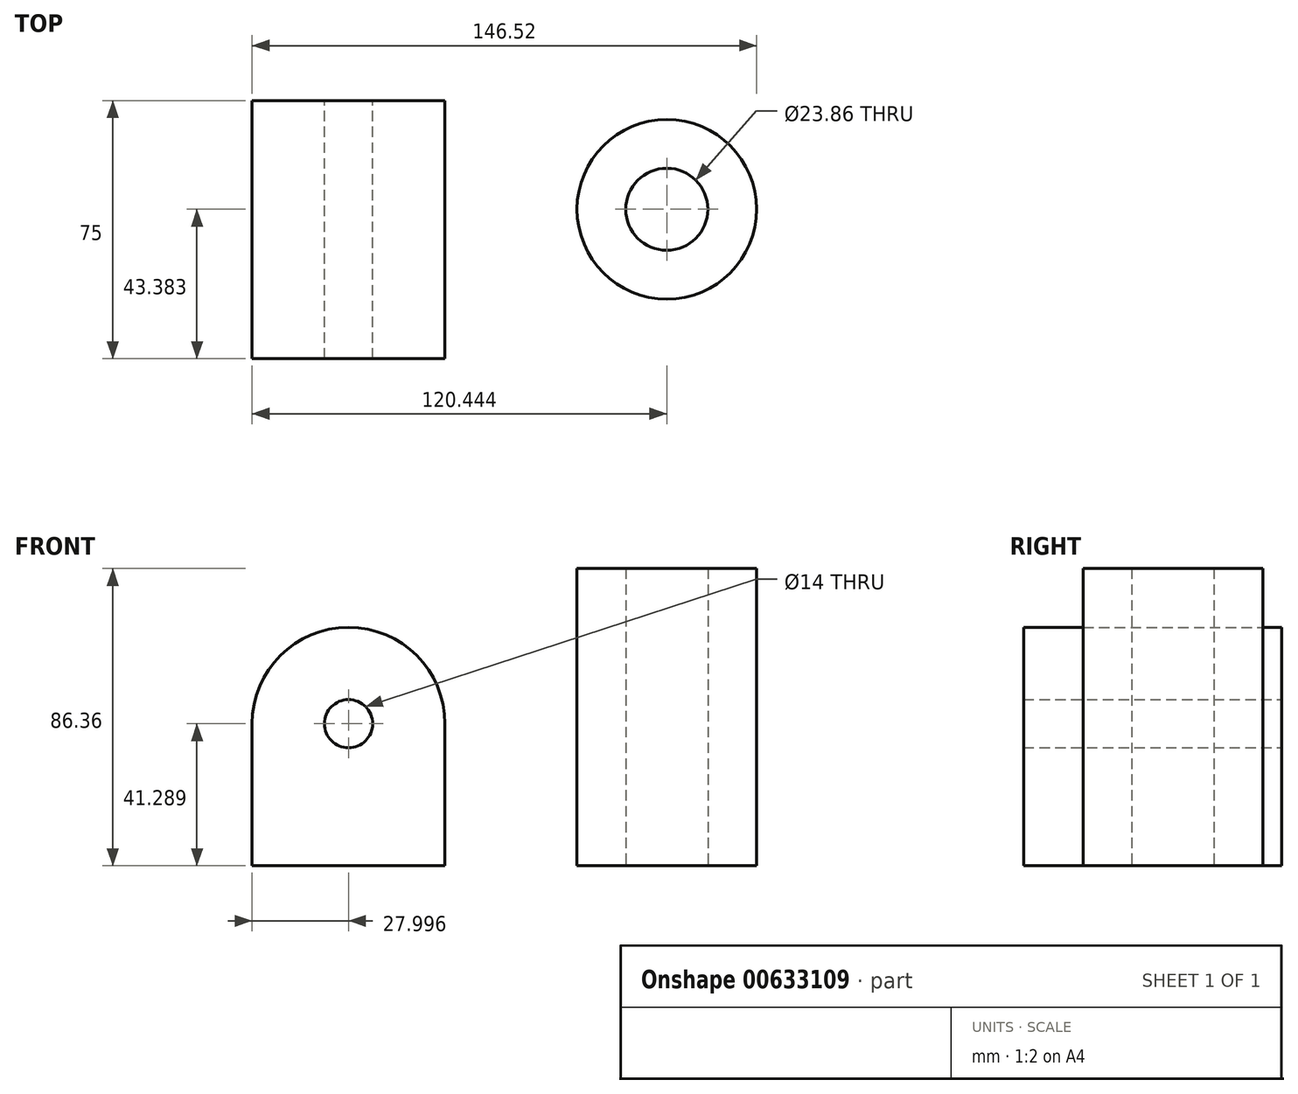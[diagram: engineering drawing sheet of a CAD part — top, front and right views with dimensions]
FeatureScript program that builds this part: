
annotation { "Feature Type Name" : "Feature", "Feature Type Description" : "" }
export const myFeature = defineFeature(function(context is Context, id is Id, definition is map)
    precondition{}
    {
        {
            var Q0;
            Q0=qCreatedBy(makeId("Front.planeOp"),FACE);
            var sketch = newSketch(context, id + "F0", { "sketchPlane" : qUnion([Q0])});
            skLineSegment(sketch, "E0", {"start": v(-66.01, -7.73) * mm, "end": v(-66.01, -49) * mm});
            skLineSegment(sketch, "E1", {"start": v(-66.01, -49) * mm, "end": v(-10.01, -49) * mm});
            skArc(sketch, "E2", {"start": v(-66.01, -7.73) * mm, "mid": v(-38.01, 20.27) * mm, "end": v(-10.01, -7.73) * mm});
            skLineSegment(sketch, "E3", {"start": v(-10.01, -7.73) * mm, "end": v(-10.01, -49) * mm});
            skCircle(sketch, "E4", {"center": v(-38.01, -7.73) * mm, "radius": 7 * mm});
            skSolve(sketch);
        }
        {
            var Q0;
            Q0=makeQuery(id+"F0.imprint","IMPRINT",FACE,{"disambiguationData":[TD([[makeQuery(id+"F0.imprint","IMPRINT",EDGE,{"derivedFrom":sQuery(id+"F0.wireOp",EDGE,"E0")}),1.0]])]});
            extrude(context, id + "F1", {"entities" : qUnion([Q0]), "depth" : 37.5 * mm, "offsetDistance" : 25.4 * mm, "hasSecondDirection" : true, "secondDirectionOppositeDirection" : true, "secondDirectionDepth" : 37.5 * mm});
        }
        {
            var Q0;
            Q0=qCreatedBy(makeId("Top.planeOp"),FACE);
            var sketch = newSketch(context, id + "F2", { "sketchPlane" : qUnion([Q0])});
            skCircle(sketch, "E5", {"center": v(54.43, 5.88) * mm, "radius": 26.08 * mm});
            skCircle(sketch, "E6", {"center": v(54.43, 5.88) * mm, "radius": 11.93 * mm});
            skSolve(sketch);
        }
        {
            var Q0;
            Q0 = qSketchRegion(id + "F2", true);
            extrude(context, id + "F3", {"entities" : qUnion([Q0]), "depth" : 37.34 * mm, "offsetDistance" : 25.4 * mm, "hasSecondDirection" : true, "secondDirectionOppositeDirection" : true, "secondDirectionDepth" : 49.02 * mm});
        }
    });
